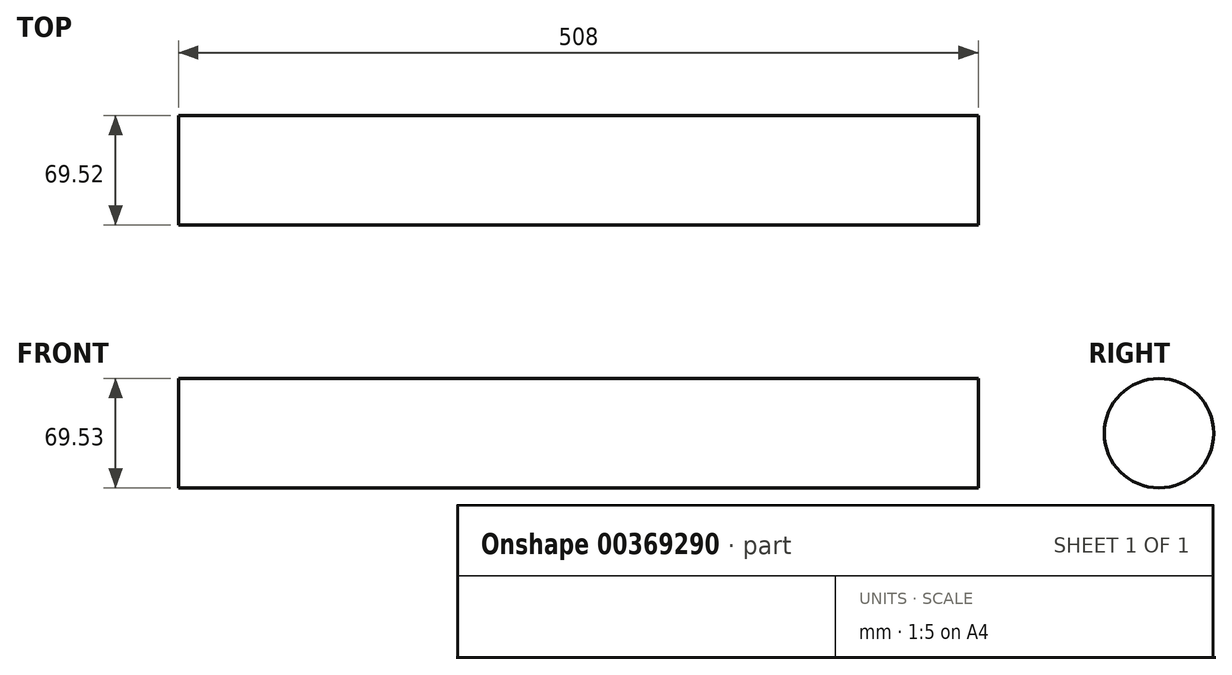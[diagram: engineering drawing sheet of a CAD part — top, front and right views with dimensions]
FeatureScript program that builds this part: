
annotation { "Feature Type Name" : "Feature", "Feature Type Description" : "" }
export const myFeature = defineFeature(function(context is Context, id is Id, definition is map)
    precondition{}
    {
        {
            var Q0;
            Q0=qCreatedBy(makeId("Front.planeOp"),FACE);
            var sketch = newSketch(context, id + "F0", { "sketchPlane" : qUnion([Q0])});
            skLineSegment(sketch, "E0.bottom", {"start": v(0, 0) * mm, "end": v(132.82, 0) * mm});
            skLineSegment(sketch, "E0.top", {"start": v(0, 131.52) * mm, "end": v(132.82, 131.52) * mm});
            skLineSegment(sketch, "E0.left", {"start": v(0, 0) * mm, "end": v(0, 131.52) * mm});
            skLineSegment(sketch, "E0.right", {"start": v(132.82, 0) * mm, "end": v(132.82, 131.52) * mm});
            skSolve(sketch);
        }
        {
            var Q0;
            Q0=sQuery(id+"F0.wireOp",EDGE,"E0.left");
            extrude(context, id + "F1", {"bodyType" : ToolBodyType.SURFACE, "surfaceEntities" : qUnion([Q0]), "depth" : 254 * mm, "hasSecondDirection" : true, "secondDirectionOppositeDirection" : true, "secondDirectionDepth" : 254 * mm});
        }
        {
            var Q0;
            Q0=makeQuery(id+"F1.opExtrude","SWEPT_FACE",FACE,{"disambiguationData":[OSD([sQuery(id+"F0.wireOp",EDGE,"E0.left")])]});
            var sketch = newSketch(context, id + "F2", { "sketchPlane" : qUnion([Q0])});
            skSolve(sketch);
        }
        {
            var Q0;
            Q0=makeQuery(id+"F2.imprint","IMPRINT",FACE,{"disambiguationData":[TD([[makeQuery(id+"F2.imprint","IMPRINT",EDGE,{"derivedFrom":makeQuery(id+"F1.opExtrude","SWEPT_EDGE",EDGE,{"disambiguationData":[OSD([sQuery(id+"F0.wireOp",VERTEX,"E0.left.start")])]})}),-1.0]])]});
            var sketch = newSketch(context, id + "F3", { "sketchPlane" : qUnion([Q0])});
            skCircle(sketch, "E1", {"center": v(0, 70.06) * mm, "radius": 34.76 * mm});
            skSolve(sketch);
        }
        {
            var Q0;
            Q0 = qSketchRegion(id + "F3", true);
            extrude(context, id + "F4", {"entities" : qUnion([Q0]), "depth" : 254 * mm, "hasSecondDirection" : true, "secondDirectionOppositeDirection" : true, "secondDirectionDepth" : 254 * mm});
        }
    });
